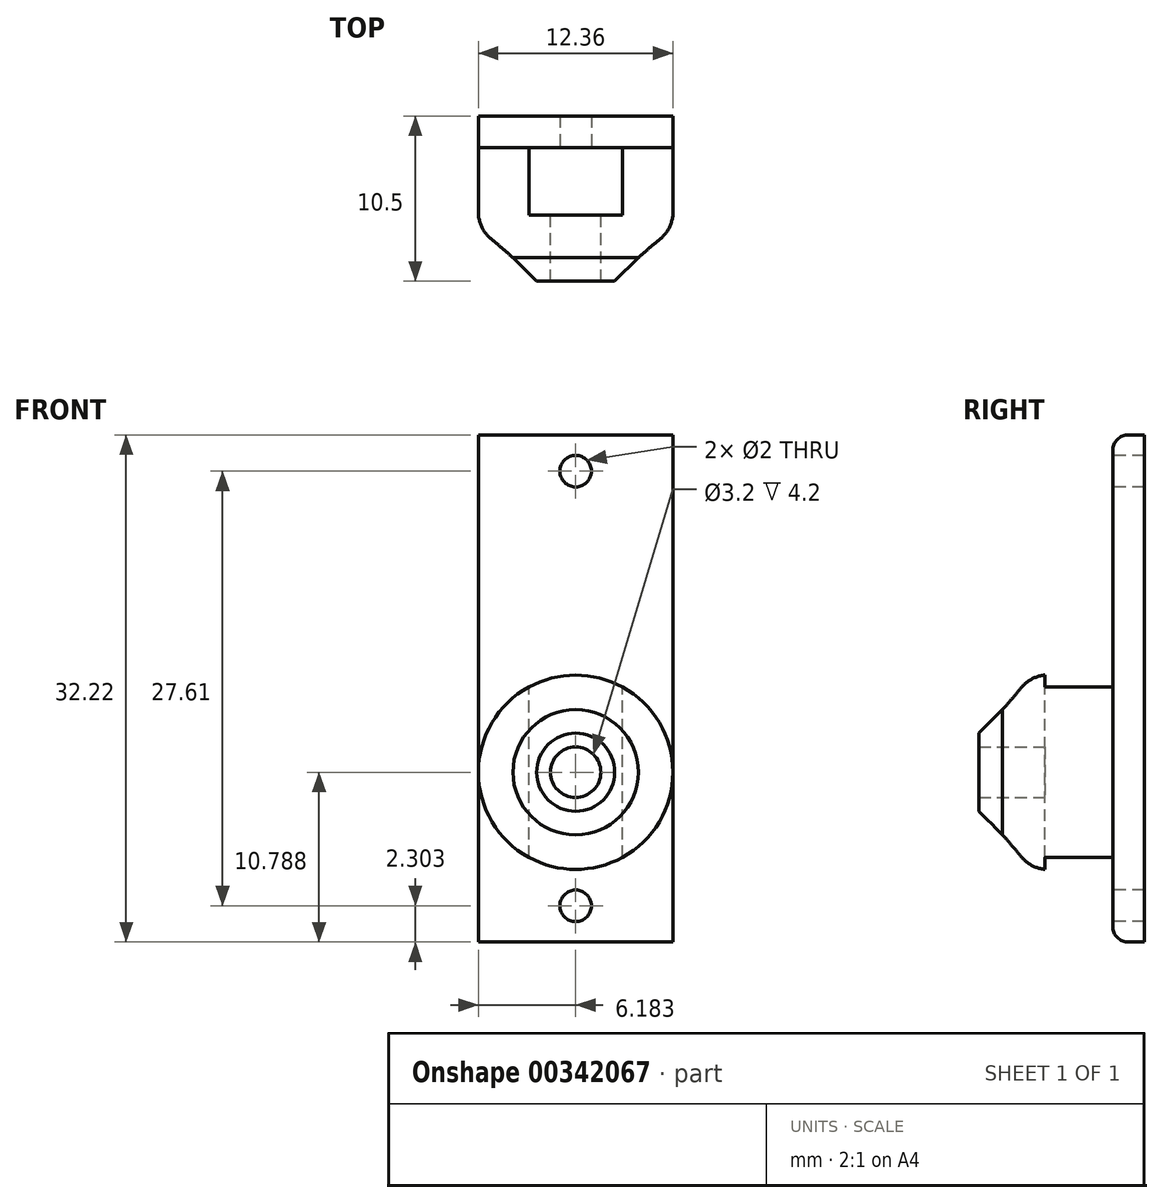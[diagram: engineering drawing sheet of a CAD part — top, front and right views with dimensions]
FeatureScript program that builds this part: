
annotation { "Feature Type Name" : "Feature", "Feature Type Description" : "" }
export const myFeature = defineFeature(function(context is Context, id is Id, definition is map)
    precondition{}
    {
        {
            var Q0;
            Q0=qCreatedBy(makeId("Front.planeOp"),FACE);
            var sketch = newSketch(context, id + "F0", { "sketchPlane" : qUnion([Q0])});
            skPoint(sketch, "E0.middle", {"position": v(0, 0) * mm});
            skLineSegment(sketch, "E1.left", {"start": v(10.15, -25.62) * mm, "end": v(10.15, 6.6) * mm});
            skLineSegment(sketch, "E1.right", {"start": v(-2.2, -25.62) * mm, "end": v(-2.2, 6.6) * mm});
            skLineSegment(sketch, "E2.left", {"start": v(-2.2, 6.6) * mm, "end": v(-2.2, -21.01) * mm});
            skLineSegment(sketch, "E2.right", {"start": v(10.15, 1.99) * mm, "end": v(10.15, -21.01) * mm});
            skCircle(sketch, "E3", {"center": v(3.97, 4.3) * mm, "radius": 1 * mm});
            skCircle(sketch, "E4", {"center": v(3.97, -14.83) * mm, "radius": 6.18 * mm});
            skCircle(sketch, "E5", {"center": v(3.97, -14.83) * mm, "radius": 1.6 * mm});
            skLineSegment(sketch, "E6.bottom", {"start": v(6.07, -16.88) * mm, "end": v(1.87, -16.88) * mm});
            skLineSegment(sketch, "E6.top", {"start": v(6.07, -12.78) * mm, "end": v(1.87, -12.78) * mm});
            skLineSegment(sketch, "E6.left", {"start": v(6.07, -16.88) * mm, "end": v(6.07, -12.78) * mm});
            skLineSegment(sketch, "E6.right", {"start": v(1.87, -16.88) * mm, "end": v(1.87, -12.78) * mm});
            skLineSegment(sketch, "E7.bottom", {"start": v(-2.2, -25.62) * mm, "end": v(10.15, -25.62) * mm});
            skLineSegment(sketch, "E7.top", {"start": v(-2.2, -21.01) * mm, "end": v(10.15, -21.01) * mm});
            skLineSegment(sketch, "E7.left", {"start": v(-2.2, -25.62) * mm, "end": v(-2.2, -21.01) * mm});
            skLineSegment(sketch, "E7.right", {"start": v(10.15, -25.62) * mm, "end": v(10.15, -21.01) * mm});
            skLineSegment(sketch, "E8.bottom", {"start": v(-2.2, 6.6) * mm, "end": v(10.15, 6.6) * mm});
            skLineSegment(sketch, "E8.top", {"start": v(-2.2, 1.99) * mm, "end": v(10.15, 1.99) * mm});
            skLineSegment(sketch, "E8.left", {"start": v(-2.2, 6.6) * mm, "end": v(-2.2, 1.99) * mm});
            skLineSegment(sketch, "E8.right", {"start": v(10.15, 6.6) * mm, "end": v(10.15, 1.99) * mm});
            skLineSegment(sketch, "E9", {"start": v(-2.2, -21.01) * mm, "end": v(10.15, -25.62) * mm, "construction": true});
            skLineSegment(sketch, "E10", {"start": v(-2.2, -25.62) * mm, "end": v(10.15, -21.01) * mm, "construction": true});
            skPoint(sketch, "E11", {"position": v(3.97, -23.32) * mm});
            skCircle(sketch, "E12", {"center": v(3.97, -23.32) * mm, "radius": 1 * mm});
            skLineSegment(sketch, "E13", {"start": v(-2.2, 6.6) * mm, "end": v(10.15, 1.99) * mm, "construction": true});
            skSolve(sketch);
        }
        {
            var Q0;
            Q0=qSketchRegion(id+"F0",true);
            var Q1;
            {var subQ4=sQuery(id+"F0.wireOp",EDGE,"cf8aaaef-a0c1-4cac-b1e5-4b45cacdd4bc.0");Q1=makeQuery(id+"F0.imprint","IMPRINT",FACE,{"disambiguationData":[TD([[makeQuery(id+"F0.imprint","IMPRINT",EDGE,{"derivedFrom":subQ4}),-1.0]])]});}
            var Q2;
            {var subQ0=sQuery(id+"F0.wireOp",EDGE,"cf8aaaef-a0c1-4cac-b1e5-4b45cacdd4bc.3");Q2=makeQuery(id+"F0.imprint","IMPRINT",FACE,{"disambiguationData":[TD([[makeQuery(id+"F0.imprint","IMPRINT",EDGE,{"derivedFrom":subQ0}),1.0]])]});}
            var Q3;
            {var subQ0=sQuery(id+"F0.wireOp",EDGE,"cf8aaaef-a0c1-4cac-b1e5-4b45cacdd4bc.4");Q3=makeQuery(id+"F0.imprint","IMPRINT",FACE,{"disambiguationData":[TD([[makeQuery(id+"F0.imprint","IMPRINT",EDGE,{"derivedFrom":subQ0}),1.0]])]});}
            var Q4;
            {var subQ0=sQuery(id+"F0.wireOp",EDGE,"cf8aaaef-a0c1-4cac-b1e5-4b45cacdd4bc.1");Q4=makeQuery(id+"F0.imprint","IMPRINT",FACE,{"disambiguationData":[TD([[makeQuery(id+"F0.imprint","IMPRINT",EDGE,{"derivedFrom":subQ0}),1.0]])]});}
            var Q5;
            {var subQ0=sQuery(id+"F0.wireOp",EDGE,"cf8aaaef-a0c1-4cac-b1e5-4b45cacdd4bc.0");Q5=makeQuery(id+"F0.imprint","IMPRINT",FACE,{"disambiguationData":[TD([[makeQuery(id+"F0.imprint","IMPRINT",EDGE,{"derivedFrom":subQ0}),1.0]])]});}
            var Q6;
            {var subQ3=sQuery(id+"F0.wireOp",EDGE,"E0.bottom");Q6=makeQuery(id+"F0.imprint","IMPRINT",FACE,{"disambiguationData":[TD([[makeQuery(id+"F0.imprint","IMPRINT",EDGE,{"derivedFrom":subQ3}),-1.0]])]});}
            var Q7;
            Q7=makeQuery(id+"F0.imprint","IMPRINT",FACE,{"disambiguationData":[TD([[makeQuery(id+"F0.imprint","IMPRINT",EDGE,{"derivedFrom":sQuery(id+"F0.wireOp",EDGE,"E5")}),1.0]])]});
            var Q8;
            Q8=makeQuery(id+"F0.imprint","IMPRINT",FACE,{"disambiguationData":[TD([[makeQuery(id+"F0.imprint","IMPRINT",EDGE,{"derivedFrom":sQuery(id+"F0.wireOp",EDGE,"E5")}),-1.0]])]});
            extrude(context, id + "F1", {"entities" : qUnion([Q0, Q1, Q2, Q3, Q4, Q5, Q6, Q7, Q8]), "oppositeDirection" : true, "depth" : 2 * mm});
        }
        {
            var Q0;
            {var subQ3=sQuery(id+"F0.wireOp",EDGE,"E0.bottom");Q0=makeQuery(id+"F0.imprint","IMPRINT",FACE,{"disambiguationData":[TD([[makeQuery(id+"F0.imprint","IMPRINT",EDGE,{"derivedFrom":subQ3}),1.0]])]});}
            var Q1;
            {var subQ3=sQuery(id+"F0.wireOp",EDGE,"E0.bottom");Q1=makeQuery(id+"F0.imprint","IMPRINT",FACE,{"disambiguationData":[TD([[makeQuery(id+"F0.imprint","IMPRINT",EDGE,{"derivedFrom":subQ3}),-1.0]])]});}
            var Q2;
            Q2=makeQuery(id+"F0.imprint","IMPRINT",FACE,{"disambiguationData":[TD([[makeQuery(id+"F0.imprint","IMPRINT",EDGE,{"derivedFrom":sQuery(id+"F0.wireOp",EDGE,"E6.bottom")}),1.0]])]});
            var Q3;
            Q3=makeQuery(id+"F0.imprint","IMPRINT",FACE,{"disambiguationData":[TD([[makeQuery(id+"F0.imprint","IMPRINT",EDGE,{"derivedFrom":sQuery(id+"F0.wireOp",EDGE,"E5")}),-1.0]])]});
            extrude(context, id + "F2", {"entities" : qUnion([Q0, Q1, Q2, Q3]), "operationType" : NewBodyOperationType.ADD, "depth" : 4.3 * mm + .9 * mm + 1.1 * mm});
        }
        {
            var Q0;
            {var subQ3=sQuery(id+"F0.wireOp",EDGE,"E0.bottom");Q0=makeQuery(id+"F0.imprint","IMPRINT",FACE,{"disambiguationData":[TD([[makeQuery(id+"F0.imprint","IMPRINT",EDGE,{"derivedFrom":subQ3}),-1.0]])]});}
            var Q1;
            Q1=makeQuery(id+"F0.imprint","IMPRINT",FACE,{"disambiguationData":[TD([[makeQuery(id+"F0.imprint","IMPRINT",EDGE,{"derivedFrom":sQuery(id+"F0.wireOp",EDGE,"E5")}),1.0]])]});
            extrude(context, id + "F3", {"entities" : qUnion([Q0, Q1]), "operationType" : NewBodyOperationType.REMOVE, "depth" : 4 * mm});
        }
        {
            var Q0;
            {var subQ0=sQuery(id+"F0.wireOp",EDGE,"E0.left");var subQ3=sQuery(id+"F0.wireOp",EDGE,"E4");Q0=makeQuery(id+"F9oB9o1exd6MhGU_1.boolean.opBoolean","SPLIT",EDGE,{"disambiguationData":[TD([makeQuery(id+"F3.boolean.opBoolean","COPY",FACE,{"derivedFrom":makeQuery(id+"F3.opExtrude","SWEPT_FACE",FACE,{"disambiguationData":[OSD([subQ0])]})})])],"derivedFrom":makeQuery(id+"F2.boolean.opBoolean","SPLIT",EDGE,{"disambiguationData":[OD(0.0)],"derivedFrom":makeQuery(id+"F2.opExtrude","CAP_EDGE",EDGE,{"disambiguationData":[OSD([subQ3])],"isStart":true})})});}
            var Q1;
            Q1=makeQuery(id+"F2.opExtrude","CAP_EDGE",EDGE,{"disambiguationData":[OSD([sQuery(id+"F0.wireOp",EDGE,"E4")])],"isStart":false});
            var Q2;
            {var subQ0=sQuery(id+"F0.wireOp",EDGE,"E0.right");var subQ3=sQuery(id+"F0.wireOp",EDGE,"E4");Q2=makeQuery(id+"F9oB9o1exd6MhGU_1.boolean.opBoolean","SPLIT",EDGE,{"disambiguationData":[TD([makeQuery(id+"F3.boolean.opBoolean","COPY",FACE,{"derivedFrom":makeQuery(id+"F3.opExtrude","SWEPT_FACE",FACE,{"disambiguationData":[OSD([subQ0])]})})])],"derivedFrom":makeQuery(id+"F2.boolean.opBoolean","SPLIT",EDGE,{"disambiguationData":[OD(0.0)],"derivedFrom":makeQuery(id+"F2.opExtrude","CAP_EDGE",EDGE,{"disambiguationData":[OSD([subQ3])],"isStart":true})})});}
            fillet(context, id + "F4", {"entities" : qUnion([Q0, Q1, Q2]), "radius" : 2.2 * mm, "tangentPropagation" : true, "allowEdgeOverflow" : false});
        }
        {
            var Q0;
            Q0=qCreatedBy(makeId("Top.planeOp"),FACE);
            var sketch = newSketch(context, id + "F5", { "sketchPlane" : qUnion([Q0])});
            skLineSegment(sketch, "E14.bottom", {"start": v(6.95, 0) * mm, "end": v(1, 0) * mm});
            skLineSegment(sketch, "E14.top", {"start": v(6.95, -4.3) * mm, "end": v(1, -4.3) * mm});
            skLineSegment(sketch, "E14.left", {"start": v(6.95, 0) * mm, "end": v(6.95, -4.3) * mm});
            skLineSegment(sketch, "E14.right", {"start": v(1, 0) * mm, "end": v(1, -4.3) * mm});
            skSolve(sketch);
        }
        {
            var Q0;
            Q0=qSketchRegion(id+"F5",true);
            extrude(context, id + "F6", {"entities" : qUnion([Q0]), "operationType" : NewBodyOperationType.REMOVE, "oppositeDirection" : true, "depth" : 25 * mm});
        }
        {
            var Q0;
            {var subQ0=sQuery(id+"F0.wireOp",EDGE,"E8.right");var subQ1=sQuery(id+"F0.wireOp",EDGE,"E8.bottom");var subQ2=sQuery(id+"F0.wireOp",EDGE,"E7.right");var subQ3=sQuery(id+"F0.wireOp",EDGE,"E2.right");Q0=makeQuery(id+"F2.boolean.opBoolean","SPLIT",EDGE,{"disambiguationData":[TD([makeQuery(id+"F1.opExtrude","SWEPT_FACE",FACE,{"disambiguationData":[OSD([subQ1])]})])],"derivedFrom":makeQuery(id+"F1.opExtrude","CAP_EDGE",EDGE,{"disambiguationData":[OSD([subQ3,subQ2,subQ0])],"isStart":true})});}
            var Q1;
            {var subQ0=sQuery(id+"F0.wireOp",EDGE,"E8.left");var subQ1=sQuery(id+"F0.wireOp",EDGE,"E8.bottom");var subQ2=sQuery(id+"F0.wireOp",EDGE,"E7.left");var subQ3=sQuery(id+"F0.wireOp",EDGE,"E2.left");Q1=makeQuery(id+"F2.boolean.opBoolean","SPLIT",EDGE,{"disambiguationData":[TD([makeQuery(id+"F1.opExtrude","SWEPT_FACE",FACE,{"disambiguationData":[OSD([subQ1])]})])],"derivedFrom":makeQuery(id+"F1.opExtrude","CAP_EDGE",EDGE,{"disambiguationData":[OSD([subQ3,subQ2,subQ0])],"isStart":true})});}
            var Q2;
            {var subQ0=sQuery(id+"F0.wireOp",EDGE,"E8.left");var subQ1=sQuery(id+"F0.wireOp",EDGE,"E7.left");var subQ2=sQuery(id+"F0.wireOp",EDGE,"E7.bottom");var subQ3=sQuery(id+"F0.wireOp",EDGE,"E2.left");Q2=makeQuery(id+"F2.boolean.opBoolean","SPLIT",EDGE,{"disambiguationData":[TD([makeQuery(id+"F1.opExtrude","SWEPT_FACE",FACE,{"disambiguationData":[OSD([subQ2])]})])],"derivedFrom":makeQuery(id+"F1.opExtrude","CAP_EDGE",EDGE,{"disambiguationData":[OSD([subQ3,subQ1,subQ0])],"isStart":true})});}
            var Q3;
            {var subQ0=sQuery(id+"F0.wireOp",EDGE,"E8.right");var subQ1=sQuery(id+"F0.wireOp",EDGE,"E7.right");var subQ2=sQuery(id+"F0.wireOp",EDGE,"E7.bottom");var subQ3=sQuery(id+"F0.wireOp",EDGE,"E2.right");Q3=makeQuery(id+"F2.boolean.opBoolean","SPLIT",EDGE,{"disambiguationData":[TD([makeQuery(id+"F1.opExtrude","SWEPT_FACE",FACE,{"disambiguationData":[OSD([subQ2])]})])],"derivedFrom":makeQuery(id+"F1.opExtrude","CAP_EDGE",EDGE,{"disambiguationData":[OSD([subQ3,subQ1,subQ0])],"isStart":true})});}
            var Q4;
            Q4=makeQuery(id+"F1.opExtrude","CAP_EDGE",EDGE,{"disambiguationData":[OSD([sQuery(id+"F0.wireOp",EDGE,"E7.bottom")])],"isStart":true});
            var Q5;
            Q5=makeQuery(id+"F1.opExtrude","CAP_EDGE",EDGE,{"disambiguationData":[OSD([sQuery(id+"F0.wireOp",EDGE,"E8.bottom")])],"isStart":true});
            fillet(context, id + "F7", {"entities" : qUnion([Q0, Q1, Q2, Q3, Q4, Q5]), "radius" : 1 * mm, "tangentPropagation" : true, "allowEdgeOverflow" : false});
        }
        {
            var Q0;
            Q0=makeQuery(id+"F2.opExtrude","CAP_FACE",FACE,{"disambiguationData":[OSD([sQuery(id+"F0.wireOp",EDGE,"E4"),sQuery(id+"F0.wireOp",EDGE,"E5")])],"isStart":false});
            var sketch = newSketch(context, id + "F8", { "sketchPlane" : qUnion([Q0])});
            skCircle(sketch, "E15", {"center": v(3.97, -14.83) * mm, "radius": 3.98 * mm});
            skCircle(sketch, "E16", {"center": v(3.97, -14.83) * mm, "radius": 1.6 * mm});
            skSolve(sketch);
        }
        {
            var Q0;
            Q0=qSketchRegion(id+"F8",true);
            extrude(context, id + "F9", {"entities" : qUnion([Q0]), "operationType" : NewBodyOperationType.ADD, "depth" : 2.2 * mm});
        }
        {
            var Q0;
            Q0=makeQuery(id+"F9.opExtrude","CAP_EDGE",EDGE,{"disambiguationData":[OSD([sQuery(id+"F8.wireOp",EDGE,"E15")])],"isStart":false});
            chamfer(context, id + "F10", {"entities" : qUnion([Q0]), "width" : 1.5 * mm, "tangentPropagation" : true});
        }
        {
            var Q0;
            {var subQ0=sQuery(id+"F0.wireOp",EDGE,"E4");Q0=makeQuery(id+"F9.boolean.opBoolean","MERGE",EDGE,{"derivedFrom":[makeQuery(id+"F4.opFillet","BLEND_EDGE",EDGE,{"blendedFrom":[makeQuery(id+"F2.opExtrude","CAP_EDGE",EDGE,{"disambiguationData":[OSD([subQ0])],"isStart":false}),makeQuery(id+"F2.opExtrude","CAP_FACE",FACE,{"disambiguationData":[OSD([subQ0,sQuery(id+"F0.wireOp",EDGE,"E5")])],"isStart":false})],"blendedInto":[makeQuery(id+"F2.opExtrude","CAP_FACE",FACE,{"disambiguationData":[OSD([subQ0,sQuery(id+"F0.wireOp",EDGE,"E5")])],"isStart":false})]}),makeQuery(id+"F9.opExtrude","CAP_EDGE",EDGE,{"disambiguationData":[OSD([sQuery(id+"F8.wireOp",EDGE,"E15")])],"isStart":true})]});}
            fillet(context, id + "F11", {"entities" : qUnion([Q0]), "radius" : 40 * mm, "tangentPropagation" : true, "allowEdgeOverflow" : false});
        }
    });
